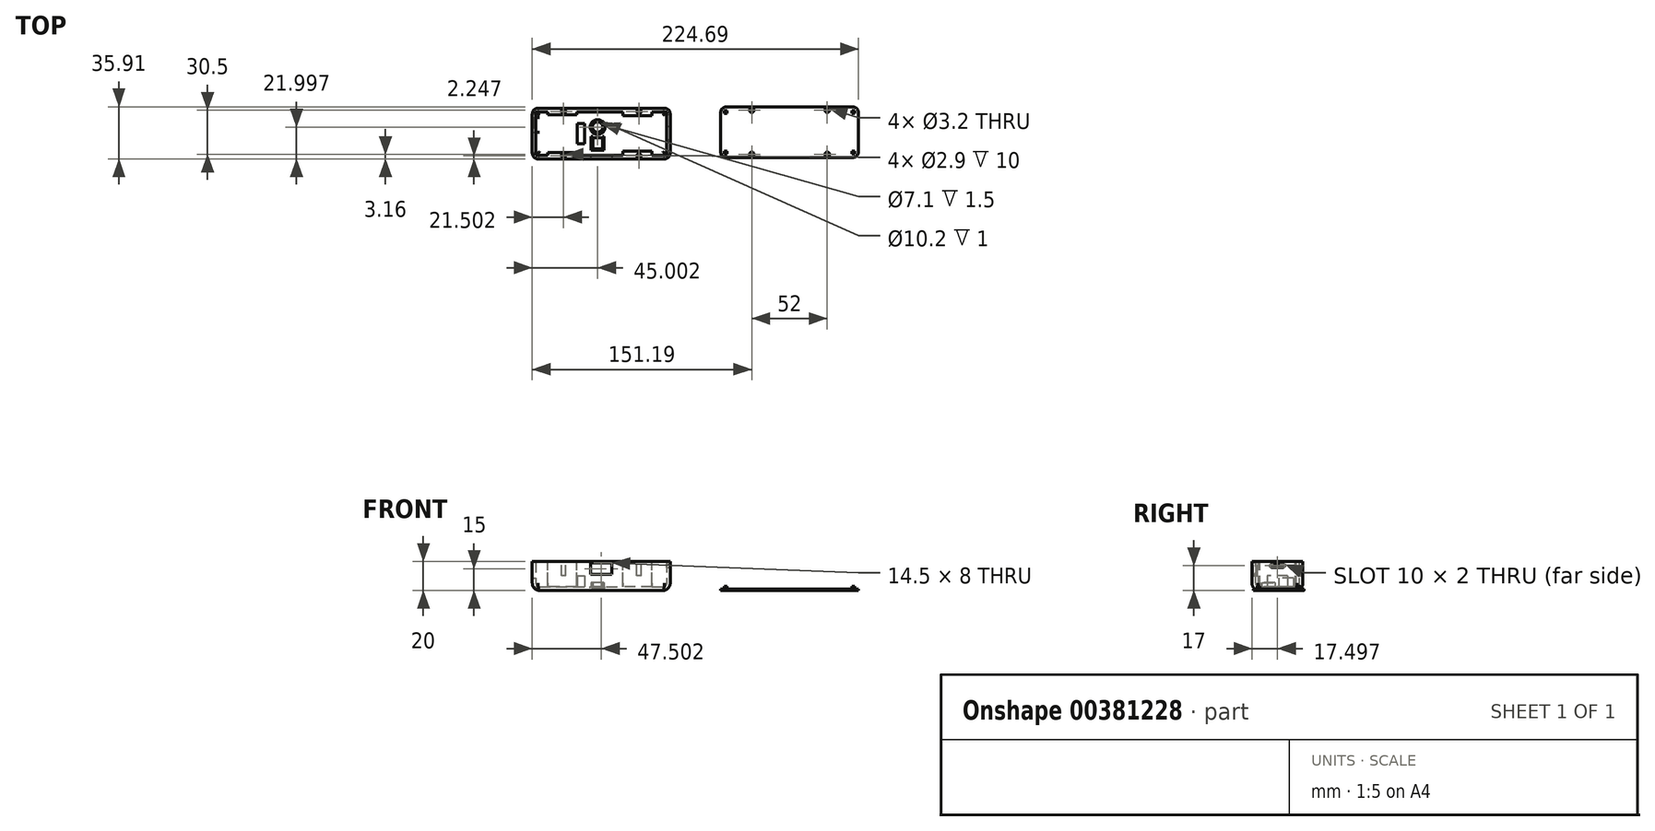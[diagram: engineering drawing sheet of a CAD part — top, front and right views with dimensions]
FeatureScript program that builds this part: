
annotation { "Feature Type Name" : "Feature", "Feature Type Description" : "" }
export const myFeature = defineFeature(function(context is Context, id is Id, definition is map)
    precondition{}
    {
        {
            var Q0;
            Q0=qCreatedBy(makeId("Top.planeOp"),FACE);
            var sketch = newSketch(context, id + "F0", { "sketchPlane" : qUnion([Q0])});
            skLineSegment(sketch, "E0.bottom", {"start": v(-57.56, 16.59) * mm, "end": v(37.44, 16.59) * mm});
            skLineSegment(sketch, "E0.top", {"start": v(-57.56, -18.41) * mm, "end": v(37.44, -18.41) * mm});
            skLineSegment(sketch, "E0.left", {"start": v(-57.56, 16.59) * mm, "end": v(-57.56, -18.41) * mm});
            skLineSegment(sketch, "E0.right", {"start": v(37.44, 16.59) * mm, "end": v(37.44, -18.41) * mm});
            skSolve(sketch);
        }
        {
            var Q0;
            Q0=makeQuery(id+"F0.imprint","IMPRINT",FACE,{"disambiguationData":[TD([[makeQuery(id+"F0.imprint","IMPRINT",EDGE,{"derivedFrom":sQuery(id+"F0.wireOp",EDGE,"E0.bottom")}),-1.0]])]});
            extrude(context, id + "F1", {"entities" : qUnion([Q0]), "depth" : 20 * mm});
        }
        {
            var Q0;
            Q0=makeQuery(id+"F1.opExtrude","CAP_FACE",FACE,{"disambiguationData":[OSD([sQuery(id+"F0.wireOp",EDGE,"E0.bottom"),sQuery(id+"F0.wireOp",EDGE,"E0.top"),sQuery(id+"F0.wireOp",EDGE,"E0.left"),sQuery(id+"F0.wireOp",EDGE,"E0.right")])],"isStart":true});
            fillet(context, id + "F2", {"entities" : qUnion([Q0]), "radius" : 5 * mm, "tangentPropagation" : true, "allowEdgeOverflow" : false});
        }
        {
            var Q0;
            Q0=makeQuery(id+"F1.opExtrude","CAP_FACE",FACE,{"disambiguationData":[OSD([sQuery(id+"F0.wireOp",EDGE,"E0.bottom"),sQuery(id+"F0.wireOp",EDGE,"E0.top"),sQuery(id+"F0.wireOp",EDGE,"E0.left"),sQuery(id+"F0.wireOp",EDGE,"E0.right")])],"isStart":false});
            shell(context, id + "F3", {"entities" : qUnion([Q0]), "thickness" : 2.5 * mm});
        }
        {
            var Q0;
            Q0=makeQuery(id+"F1.opExtrude","SWEPT_EDGE",EDGE,{"disambiguationData":[OSD([sQuery(id+"F0.wireOp",EDGE,"E0.bottom"),sQuery(id+"F0.wireOp",EDGE,"E0.left")])]});
            var Q1;
            Q1=makeQuery(id+"F1.opExtrude","SWEPT_EDGE",EDGE,{"disambiguationData":[OSD([sQuery(id+"F0.wireOp",EDGE,"E0.top"),sQuery(id+"F0.wireOp",EDGE,"E0.left")])]});
            var Q2;
            Q2=makeQuery(id+"F1.opExtrude","SWEPT_EDGE",EDGE,{"disambiguationData":[OSD([sQuery(id+"F0.wireOp",EDGE,"E0.top"),sQuery(id+"F0.wireOp",EDGE,"E0.right")])]});
            var Q3;
            Q3=makeQuery(id+"F1.opExtrude","SWEPT_EDGE",EDGE,{"disambiguationData":[OSD([sQuery(id+"F0.wireOp",EDGE,"E0.bottom"),sQuery(id+"F0.wireOp",EDGE,"E0.right")])]});
            fillet(context, id + "F4", {"entities" : qUnion([Q0, Q1, Q2, Q3]), "radius" : 4 * mm, "tangentPropagation" : true, "allowEdgeOverflow" : false});
        }
        {
            var Q0;
            Q0=makeQuery(id+"F1.opExtrude","CAP_FACE",FACE,{"disambiguationData":[OSD([sQuery(id+"F0.wireOp",EDGE,"E0.bottom"),sQuery(id+"F0.wireOp",EDGE,"E0.top"),sQuery(id+"F0.wireOp",EDGE,"E0.left"),sQuery(id+"F0.wireOp",EDGE,"E0.right")])],"isStart":false});
            var sketch = newSketch(context, id + "F5", { "sketchPlane" : qUnion([Q0])});
            skLineSegment(sketch, "E1.bottom", {"start": v(-47.06, 14.09) * mm, "end": v(-27.06, 14.09) * mm});
            skLineSegment(sketch, "E1.top", {"start": v(-47.06, 12.09) * mm, "end": v(-27.06, 12.09) * mm});
            skLineSegment(sketch, "E1.left", {"start": v(-47.06, 14.09) * mm, "end": v(-47.06, 12.09) * mm});
            skLineSegment(sketch, "E1.right", {"start": v(-27.06, 14.09) * mm, "end": v(-27.06, 12.09) * mm});
            skLineSegment(sketch, "E2.bottom", {"start": v(-47.06, -15.91) * mm, "end": v(-27.06, -15.91) * mm});
            skLineSegment(sketch, "E2.top", {"start": v(-47.06, -13.91) * mm, "end": v(-27.06, -13.91) * mm});
            skLineSegment(sketch, "E2.left", {"start": v(-47.06, -15.91) * mm, "end": v(-47.06, -13.91) * mm});
            skLineSegment(sketch, "E2.right", {"start": v(-27.06, -15.91) * mm, "end": v(-27.06, -13.91) * mm});
            skLineSegment(sketch, "E3.bottom", {"start": v(4.94, 14.09) * mm, "end": v(24.94, 14.09) * mm});
            skLineSegment(sketch, "E3.top", {"start": v(4.94, 11.34) * mm, "end": v(24.94, 11.34) * mm});
            skLineSegment(sketch, "E3.left", {"start": v(4.94, 14.09) * mm, "end": v(4.94, 11.34) * mm});
            skLineSegment(sketch, "E3.right", {"start": v(24.94, 14.09) * mm, "end": v(24.94, 11.34) * mm});
            skLineSegment(sketch, "E4.bottom", {"start": v(4.94, -15.91) * mm, "end": v(24.94, -15.91) * mm});
            skLineSegment(sketch, "E4.top", {"start": v(4.94, -13.16) * mm, "end": v(24.94, -13.16) * mm});
            skLineSegment(sketch, "E4.left", {"start": v(4.94, -15.91) * mm, "end": v(4.94, -13.16) * mm});
            skLineSegment(sketch, "E4.right", {"start": v(24.94, -15.91) * mm, "end": v(24.94, -13.16) * mm});
            skSolve(sketch);
        }
        {
            var Q0;
            Q0=makeQuery(id+"F5.imprint","IMPRINT",FACE,{"disambiguationData":[TD([[makeQuery(id+"F5.imprint","IMPRINT",EDGE,{"derivedFrom":sQuery(id+"F5.wireOp",EDGE,"E1.bottom")}),-1.0]])]});
            var Q1;
            Q1=makeQuery(id+"F5.imprint","IMPRINT",FACE,{"disambiguationData":[TD([[makeQuery(id+"F5.imprint","IMPRINT",EDGE,{"derivedFrom":sQuery(id+"F5.wireOp",EDGE,"E2.bottom")}),1.0]])]});
            var Q2;
            Q2=makeQuery(id+"F5.imprint","IMPRINT",FACE,{"disambiguationData":[TD([[makeQuery(id+"F5.imprint","IMPRINT",EDGE,{"derivedFrom":sQuery(id+"F5.wireOp",EDGE,"E4.bottom")}),1.0]])]});
            var Q3;
            Q3=makeQuery(id+"F5.imprint","IMPRINT",FACE,{"disambiguationData":[TD([[makeQuery(id+"F5.imprint","IMPRINT",EDGE,{"derivedFrom":sQuery(id+"F5.wireOp",EDGE,"E3.bottom")}),-1.0]])]});
            extrude(context, id + "F6", {"entities" : qUnion([Q0, Q1, Q2, Q3]), "operationType" : NewBodyOperationType.ADD, "endBound" : BoundingType.UP_TO_NEXT, "oppositeDirection" : true, "depth" : 25 * mm});
        }
        {
            var Q0;
            Q0=makeQuery(id+"F3.opShell","OFFSET_FACE",FACE,{"disambiguationData":[OSD([sQuery(id+"F0.wireOp",EDGE,"E0.bottom"),sQuery(id+"F0.wireOp",EDGE,"E0.top"),sQuery(id+"F0.wireOp",EDGE,"E0.left"),sQuery(id+"F0.wireOp",EDGE,"E0.right")])]});
            var sketch = newSketch(context, id + "F7", { "sketchPlane" : qUnion([Q0])});
            skLineSegment(sketch, "E5", {"start": v(-12.56, 11.59) * mm, "end": v(-12.56, -13.41) * mm, "construction": true});
            skCircle(sketch, "E6", {"center": v(-12.56, 3.59) * mm, "radius": 3.55 * mm});
            skLineSegment(sketch, "E7.bottom", {"start": v(-9.16, -11.41) * mm, "end": v(-15.96, -11.41) * mm});
            skLineSegment(sketch, "E7.top", {"start": v(-9.16, -3.71) * mm, "end": v(-15.96, -3.71) * mm});
            skLineSegment(sketch, "E7.left", {"start": v(-9.16, -11.41) * mm, "end": v(-9.16, -3.71) * mm});
            skLineSegment(sketch, "E7.right", {"start": v(-15.96, -11.41) * mm, "end": v(-15.96, -3.71) * mm});
            skPoint(sketch, "E7.middle", {"position": v(-12.56, -7.56) * mm});
            skLineSegment(sketch, "E8.bottom", {"start": v(-8.16, -2.71) * mm, "end": v(-9.16, -2.71) * mm});
            skLineSegment(sketch, "E8.top", {"start": v(-8.16, -12.41) * mm, "end": v(-16.96, -12.41) * mm});
            skLineSegment(sketch, "E8.left", {"start": v(-8.16, -2.71) * mm, "end": v(-8.16, -12.41) * mm});
            skLineSegment(sketch, "E8.right", {"start": v(-16.96, -2.71) * mm, "end": v(-16.96, -12.41) * mm});
            skLineSegment(sketch, "E9", {"start": v(-15.96, -3.71) * mm, "end": v(-15.96, -2.71) * mm});
            skLineSegment(sketch, "E10", {"start": v(-9.16, -3.71) * mm, "end": v(-9.16, -2.71) * mm});
            skLineSegment(sketch, "E11.trimOffspring", {"start": v(-15.96, -2.71) * mm, "end": v(-16.96, -2.71) * mm});
            skCircle(sketch, "E12", {"center": v(-12.56, 3.59) * mm, "radius": 5.1 * mm});
            skLineSegment(sketch, "E13.bottom", {"start": v(-26.56, 6.09) * mm, "end": v(-21.56, 6.09) * mm});
            skLineSegment(sketch, "E13.top", {"start": v(-26.56, -7.91) * mm, "end": v(-21.56, -7.91) * mm});
            skLineSegment(sketch, "E13.left", {"start": v(-26.56, 6.09) * mm, "end": v(-26.56, -7.91) * mm});
            skLineSegment(sketch, "E13.right", {"start": v(-21.56, 6.09) * mm, "end": v(-21.56, -7.91) * mm});
            skPoint(sketch, "E14", {"position": v(-26.56, -0.91) * mm});
            skPoint(sketch, "E15", {"position": v(-21.56, -0.91) * mm});
            skLineSegment(sketch, "E16", {"start": v(-52.56, -0.91) * mm, "end": v(-26.56, -0.91) * mm, "construction": true});
            skSolve(sketch);
        }
        {
            var Q0;
            Q0=makeQuery(id+"F7.imprint","IMPRINT",FACE,{"disambiguationData":[TD([[makeQuery(id+"F7.imprint","IMPRINT",EDGE,{"derivedFrom":sQuery(id+"F7.wireOp",EDGE,"E6")}),1.0]])]});
            var Q1;
            Q1=makeQuery(id+"F7.imprint","IMPRINT",FACE,{"disambiguationData":[TD([[makeQuery(id+"F7.imprint","IMPRINT",EDGE,{"derivedFrom":sQuery(id+"F7.wireOp",EDGE,"E7.bottom")}),-1.0]])]});
            extrude(context, id + "F8", {"entities" : qUnion([Q0, Q1]), "operationType" : NewBodyOperationType.REMOVE, "endBound" : BoundingType.UP_TO_NEXT, "oppositeDirection" : true, "depth" : 25 * mm});
        }
        {
            var Q0;
            Q0=makeQuery(id+"F7.imprint","IMPRINT",FACE,{"disambiguationData":[TD([[makeQuery(id+"F7.imprint","IMPRINT",EDGE,{"derivedFrom":sQuery(id+"F7.wireOp",EDGE,"E6")}),-1.0]])]});
            extrude(context, id + "F9", {"entities" : qUnion([Q0]), "operationType" : NewBodyOperationType.REMOVE, "oppositeDirection" : true, "depth" : 1 * mm});
        }
        {
            var Q0;
            Q0=makeQuery(id+"F7.imprint","IMPRINT",FACE,{"disambiguationData":[TD([[makeQuery(id+"F7.imprint","IMPRINT",EDGE,{"derivedFrom":sQuery(id+"F7.wireOp",EDGE,"E7.bottom")}),1.0]])]});
            extrude(context, id + "F10", {"entities" : qUnion([Q0]), "operationType" : NewBodyOperationType.ADD, "depth" : 3 * mm});
        }
        {
            var Q0;
            Q0=makeQuery(id+"F7.imprint","IMPRINT",FACE,{"disambiguationData":[TD([[makeQuery(id+"F7.imprint","IMPRINT",EDGE,{"derivedFrom":sQuery(id+"F7.wireOp",EDGE,"E13.bottom")}),-1.0]])]});
            extrude(context, id + "F11", {"entities" : qUnion([Q0]), "operationType" : NewBodyOperationType.ADD, "depth" : 7.6 * mm});
        }
        {
            var Q0;
            Q0=makeQuery(id+"F6.opExtrude","SWEPT_FACE",FACE,{"disambiguationData":[OSD([sQuery(id+"F5.wireOp",EDGE,"E1.left")])]});
            var sketch = newSketch(context, id + "F12", { "sketchPlane" : qUnion([Q0])});
            skLineSegment(sketch, "E17.bottom", {"start": v(-10.09, 8.5) * mm, "end": v(-0.09, 8.5) * mm});
            skLineSegment(sketch, "E17.top", {"start": v(-10.09, 2.5) * mm, "end": v(-0.09, 2.5) * mm});
            skLineSegment(sketch, "E17.left", {"start": v(-10.09, 8.5) * mm, "end": v(-10.09, 2.5) * mm});
            skLineSegment(sketch, "E17.right", {"start": v(-0.09, 8.5) * mm, "end": v(-0.09, 2.5) * mm});
            skSolve(sketch);
        }
        {
            var Q0;
            Q0=makeQuery(id+"F12.imprint","IMPRINT",FACE,{"disambiguationData":[TD([[makeQuery(id+"F12.imprint","IMPRINT",EDGE,{"derivedFrom":sQuery(id+"F12.wireOp",EDGE,"E17.bottom")}),-1.0]])]});
            extrude(context, id + "F13", {"entities" : qUnion([Q0]), "operationType" : NewBodyOperationType.REMOVE, "depth" : 13.3 * mm});
        }
        {
            var Q0;
            Q0=makeQuery(id+"F1.opExtrude","SWEPT_FACE",FACE,{"disambiguationData":[OSD([sQuery(id+"F0.wireOp",EDGE,"E0.right")])]});
            var sketch = newSketch(context, id + "F14", { "sketchPlane" : qUnion([Q0])});
            skLineSegment(sketch, "E18", {"start": v(12.59, 17) * mm, "end": v(-14.41, 17) * mm, "construction": true});
            skArc(sketch, "E19", {"start": v(3.09, 16) * mm, "mid": v(4.09, 17) * mm, "end": v(3.09, 18) * mm});
            skArc(sketch, "E20", {"start": v(-4.91, 18) * mm, "mid": v(-5.91, 16.97) * mm, "end": v(-4.86, 16) * mm});
            skLineSegment(sketch, "E21", {"start": v(3.09, 18) * mm, "end": v(-4.91, 18) * mm});
            skLineSegment(sketch, "E22", {"start": v(-4.97, 16) * mm, "end": v(3.09, 16) * mm});
            skLineSegment(sketch, "E23", {"start": v(-0.91, 18) * mm, "end": v(-0.91, 20) * mm, "construction": true});
            skSolve(sketch);
        }
        {
            var Q0;
            {var subQ5=sQuery(id+"F14.wireOp",EDGE,"E19");Q0=makeQuery(id+"F14.imprint","IMPRINT",FACE,{"disambiguationData":[TD([[makeQuery(id+"F14.imprint","IMPRINT",EDGE,{"derivedFrom":subQ5}),1.0]])]});}
            extrude(context, id + "F15", {"entities" : qUnion([Q0]), "operationType" : NewBodyOperationType.REMOVE, "endBound" : BoundingType.UP_TO_NEXT, "oppositeDirection" : true, "depth" : 25 * mm});
        }
        {
            var Q0;
            Q0=makeQuery(id+"F6.boolean.opBoolean","MERGE",FACE,{"derivedFrom":[makeQuery(id+"F1.opExtrude","CAP_FACE",FACE,{"disambiguationData":[OSD([sQuery(id+"F0.wireOp",EDGE,"E0.bottom"),sQuery(id+"F0.wireOp",EDGE,"E0.top"),sQuery(id+"F0.wireOp",EDGE,"E0.left"),sQuery(id+"F0.wireOp",EDGE,"E0.right")])],"isStart":false}),makeQuery(id+"F6.opExtrude","CAP_FACE",FACE,{"disambiguationData":[OSD([sQuery(id+"F5.wireOp",EDGE,"E1.bottom"),sQuery(id+"F5.wireOp",EDGE,"E1.top"),sQuery(id+"F5.wireOp",EDGE,"E1.left"),sQuery(id+"F5.wireOp",EDGE,"E1.right")])],"isStart":true}),makeQuery(id+"F6.opExtrude","CAP_FACE",FACE,{"disambiguationData":[OSD([sQuery(id+"F5.wireOp",EDGE,"E2.bottom"),sQuery(id+"F5.wireOp",EDGE,"E2.top"),sQuery(id+"F5.wireOp",EDGE,"E2.left"),sQuery(id+"F5.wireOp",EDGE,"E2.right")])],"isStart":true}),makeQuery(id+"F6.opExtrude","CAP_FACE",FACE,{"disambiguationData":[OSD([sQuery(id+"F5.wireOp",EDGE,"E3.bottom"),sQuery(id+"F5.wireOp",EDGE,"E3.top"),sQuery(id+"F5.wireOp",EDGE,"E3.left"),sQuery(id+"F5.wireOp",EDGE,"E3.right")])],"isStart":true}),makeQuery(id+"F6.opExtrude","CAP_FACE",FACE,{"disambiguationData":[OSD([sQuery(id+"F5.wireOp",EDGE,"E4.bottom"),sQuery(id+"F5.wireOp",EDGE,"E4.top"),sQuery(id+"F5.wireOp",EDGE,"E4.left"),sQuery(id+"F5.wireOp",EDGE,"E4.right")])],"isStart":true})]});
            var sketch = newSketch(context, id + "F16", { "sketchPlane" : qUnion([Q0])});
            skCircle(sketch, "E24", {"center": v(-36.06, 14.34) * mm, "radius": 1.45 * mm});
            skCircle(sketch, "E25", {"center": v(-36.06, -16.16) * mm, "radius": 1.45 * mm});
            skCircle(sketch, "E26", {"center": v(15.94, -16.16) * mm, "radius": 1.45 * mm});
            skCircle(sketch, "E27", {"center": v(15.94, 14.34) * mm, "radius": 1.45 * mm});
            skLineSegment(sketch, "E28", {"start": v(-36.06, 14.34) * mm, "end": v(-36.06, -16.16) * mm, "construction": true});
            skLineSegment(sketch, "E29", {"start": v(15.94, 14.34) * mm, "end": v(15.94, -16.16) * mm, "construction": true});
            skLineSegment(sketch, "E30", {"start": v(-10.06, 16.59) * mm, "end": v(-10.06, -18.41) * mm, "construction": true});
            skLineSegment(sketch, "E31", {"start": v(-36.06, 14.34) * mm, "end": v(15.94, 14.34) * mm, "construction": true});
            skLineSegment(sketch, "E32", {"start": v(-36.06, -16.16) * mm, "end": v(15.94, -16.16) * mm, "construction": true});
            skLineSegment(sketch, "E33", {"start": v(-36.06, 14.34) * mm, "end": v(-36.06, 16.59) * mm, "construction": true});
            skLineSegment(sketch, "E34", {"start": v(-36.06, -16.16) * mm, "end": v(-36.06, -18.41) * mm, "construction": true});
            skSolve(sketch);
        }
        {
            var Q0;
            Q0=makeQuery(id+"F16.imprint","IMPRINT",FACE,{"disambiguationData":[TD([[makeQuery(id+"F16.imprint","IMPRINT",EDGE,{"derivedFrom":sQuery(id+"F16.wireOp",EDGE,"E24")}),1.0]])]});
            var Q1;
            Q1=makeQuery(id+"F16.imprint","IMPRINT",FACE,{"disambiguationData":[TD([[makeQuery(id+"F16.imprint","IMPRINT",EDGE,{"derivedFrom":sQuery(id+"F16.wireOp",EDGE,"E25")}),1.0]])]});
            var Q2;
            Q2=makeQuery(id+"F16.imprint","IMPRINT",FACE,{"disambiguationData":[TD([[makeQuery(id+"F16.imprint","IMPRINT",EDGE,{"derivedFrom":sQuery(id+"F16.wireOp",EDGE,"E26")}),1.0]])]});
            var Q3;
            Q3=makeQuery(id+"F16.imprint","IMPRINT",FACE,{"disambiguationData":[TD([[makeQuery(id+"F16.imprint","IMPRINT",EDGE,{"derivedFrom":sQuery(id+"F16.wireOp",EDGE,"E27")}),1.0]])]});
            extrude(context, id + "F17", {"entities" : qUnion([Q0, Q1, Q2, Q3]), "operationType" : NewBodyOperationType.REMOVE, "oppositeDirection" : true, "depth" : 10 * mm});
        }
        {
            var Q0;
            Q0=makeQuery(id+"F1.opExtrude","SWEPT_FACE",FACE,{"disambiguationData":[OSD([sQuery(id+"F0.wireOp",EDGE,"E0.top")])]});
            var sketch = newSketch(context, id + "F18", { "sketchPlane" : qUnion([Q0])});
            skLineSegment(sketch, "E35", {"start": v(-10.06, 20) * mm, "end": v(-10.06, 5) * mm, "construction": true});
            skLineSegment(sketch, "E36.bottom", {"start": v(-2.8, 19) * mm, "end": v(-17.3, 19) * mm});
            skLineSegment(sketch, "E36.top", {"start": v(-2.8, 11) * mm, "end": v(-17.3, 11) * mm});
            skLineSegment(sketch, "E36.left", {"start": v(-2.8, 19) * mm, "end": v(-2.8, 11) * mm});
            skLineSegment(sketch, "E36.right", {"start": v(-17.3, 19) * mm, "end": v(-17.3, 11) * mm});
            skPoint(sketch, "E36.middle", {"position": v(-10.06, 15) * mm});
            skSolve(sketch);
        }
        {
            var Q0;
            Q0 = qSketchRegion(id + "F18", true);
            extrude(context, id + "F19", {"entities" : qUnion([Q0]), "operationType" : NewBodyOperationType.REMOVE, "endBound" : BoundingType.UP_TO_NEXT, "oppositeDirection" : true, "depth" : 25 * mm});
        }
        {
            var Q0;
            Q0=qCreatedBy(makeId("Top.planeOp"),FACE);
            var sketch = newSketch(context, id + "F20", { "sketchPlane" : qUnion([Q0])});
            skLineSegment(sketch, "E37.bottom", {"start": v(76.13, 17.5) * mm, "end": v(163.13, 17.5) * mm});
            skLineSegment(sketch, "E37.top", {"start": v(76.13, -17.5) * mm, "end": v(163.13, -17.5) * mm});
            skLineSegment(sketch, "E37.left", {"start": v(72.13, 13.5) * mm, "end": v(72.13, -13.5) * mm});
            skLineSegment(sketch, "E37.right", {"start": v(167.13, 13.5) * mm, "end": v(167.13, -13.5) * mm});
            skPoint(sketch, "E37.middle", {"position": v(119.63, 0) * mm});
            skPoint(sketch, "E38.visualSharp", {"position": v(72.13, 17.5) * mm});
            skArc(sketch, "E38.filletArc", {"start": v(76.13, 17.5) * mm, "mid": v(73.3, 16.33) * mm, "end": v(72.13, 13.5) * mm});
            skPoint(sketch, "E39.visualSharp", {"position": v(72.13, -17.5) * mm});
            skArc(sketch, "E39.filletArc", {"start": v(72.13, -13.5) * mm, "mid": v(73.3, -16.33) * mm, "end": v(76.13, -17.5) * mm});
            skPoint(sketch, "E40.visualSharp", {"position": v(167.13, -17.5) * mm});
            skArc(sketch, "E40.filletArc", {"start": v(163.13, -17.5) * mm, "mid": v(165.96, -16.33) * mm, "end": v(167.13, -13.5) * mm});
            skPoint(sketch, "E41.visualSharp", {"position": v(167.13, 17.5) * mm});
            skArc(sketch, "E41.filletArc", {"start": v(167.13, 13.5) * mm, "mid": v(165.96, 16.33) * mm, "end": v(163.13, 17.5) * mm});
            skSolve(sketch);
        }
        {
            var Q0;
            Q0=makeQuery(id+"F20.imprint","IMPRINT",FACE,{"disambiguationData":[TD([[makeQuery(id+"F20.imprint","IMPRINT",EDGE,{"derivedFrom":sQuery(id+"F20.wireOp",EDGE,"E37.bottom")}),-1.0]])]});
            extrude(context, id + "F21", {"entities" : qUnion([Q0]), "depth" : 1 * mm});
        }
        {
            var Q0;
            Q0=makeQuery(id+"F21.opExtrude","CAP_FACE",FACE,{"disambiguationData":[OSD([sQuery(id+"F20.wireOp",EDGE,"E37.bottom"),sQuery(id+"F20.wireOp",EDGE,"E37.top"),sQuery(id+"F20.wireOp",EDGE,"E37.left"),sQuery(id+"F20.wireOp",EDGE,"E37.right"),sQuery(id+"F20.wireOp",EDGE,"E38.filletArc"),sQuery(id+"F20.wireOp",EDGE,"E39.filletArc"),sQuery(id+"F20.wireOp",EDGE,"E40.filletArc"),sQuery(id+"F20.wireOp",EDGE,"E41.filletArc")])],"isStart":false});
            var sketch = newSketch(context, id + "F22", { "sketchPlane" : qUnion([Q0])});
            skLineSegment(sketch, "E42.bottom", {"start": v(74.73, 14.9) * mm, "end": v(76.73, 14.9) * mm});
            skLineSegment(sketch, "E42.top", {"start": v(74.73, 12.9) * mm, "end": v(76.73, 12.9) * mm});
            skLineSegment(sketch, "E42.left", {"start": v(74.73, 14.9) * mm, "end": v(74.73, 12.9) * mm});
            skLineSegment(sketch, "E42.right", {"start": v(76.73, 14.9) * mm, "end": v(76.73, 12.9) * mm});
            skLineSegment(sketch, "E43.bottom", {"start": v(74.73, -14.9) * mm, "end": v(76.73, -14.9) * mm});
            skLineSegment(sketch, "E43.top", {"start": v(74.73, -12.9) * mm, "end": v(76.73, -12.9) * mm});
            skLineSegment(sketch, "E43.left", {"start": v(74.73, -14.9) * mm, "end": v(74.73, -12.9) * mm});
            skLineSegment(sketch, "E43.right", {"start": v(76.73, -14.9) * mm, "end": v(76.73, -12.9) * mm});
            skLineSegment(sketch, "E44.bottom", {"start": v(164.53, -14.9) * mm, "end": v(162.53, -14.9) * mm});
            skLineSegment(sketch, "E44.top", {"start": v(164.53, -12.9) * mm, "end": v(162.53, -12.9) * mm});
            skLineSegment(sketch, "E44.left", {"start": v(164.53, -14.9) * mm, "end": v(164.53, -12.9) * mm});
            skLineSegment(sketch, "E44.right", {"start": v(162.53, -14.9) * mm, "end": v(162.53, -12.9) * mm});
            skLineSegment(sketch, "E45.bottom", {"start": v(164.53, 14.9) * mm, "end": v(162.53, 14.9) * mm});
            skLineSegment(sketch, "E45.top", {"start": v(164.53, 12.9) * mm, "end": v(162.53, 12.9) * mm});
            skLineSegment(sketch, "E45.left", {"start": v(164.53, 14.9) * mm, "end": v(164.53, 12.9) * mm});
            skLineSegment(sketch, "E45.right", {"start": v(162.53, 14.9) * mm, "end": v(162.53, 12.9) * mm});
            skLineSegment(sketch, "E46", {"start": v(76.73, 14.9) * mm, "end": v(162.53, 14.9) * mm, "construction": true});
            skLineSegment(sketch, "E47", {"start": v(76.73, -14.9) * mm, "end": v(162.53, -14.9) * mm, "construction": true});
            skLineSegment(sketch, "E48", {"start": v(74.73, 12.9) * mm, "end": v(74.73, -12.9) * mm, "construction": true});
            skLineSegment(sketch, "E49", {"start": v(164.53, 12.9) * mm, "end": v(164.53, -12.9) * mm, "construction": true});
            skSolve(sketch);
        }
        {
            var Q0;
            Q0=makeQuery(id+"F22.imprint","IMPRINT",FACE,{"disambiguationData":[TD([[makeQuery(id+"F22.imprint","IMPRINT",EDGE,{"derivedFrom":sQuery(id+"F22.wireOp",EDGE,"E42.bottom")}),-1.0]])]});
            var Q1;
            Q1=makeQuery(id+"F22.imprint","IMPRINT",FACE,{"disambiguationData":[TD([[makeQuery(id+"F22.imprint","IMPRINT",EDGE,{"derivedFrom":sQuery(id+"F22.wireOp",EDGE,"E43.bottom")}),1.0]])]});
            var Q2;
            Q2=makeQuery(id+"F22.imprint","IMPRINT",FACE,{"disambiguationData":[TD([[makeQuery(id+"F22.imprint","IMPRINT",EDGE,{"derivedFrom":sQuery(id+"F22.wireOp",EDGE,"E44.bottom")}),-1.0]])]});
            var Q3;
            Q3=makeQuery(id+"F22.imprint","IMPRINT",FACE,{"disambiguationData":[TD([[makeQuery(id+"F22.imprint","IMPRINT",EDGE,{"derivedFrom":sQuery(id+"F22.wireOp",EDGE,"E45.bottom")}),1.0]])]});
            extrude(context, id + "F23", {"entities" : qUnion([Q0, Q1, Q2, Q3]), "operationType" : NewBodyOperationType.ADD, "depth" : 2 * mm});
        }
        {
            var Q0;
            Q0=makeQuery(id+"F21.opExtrude","CAP_FACE",FACE,{"disambiguationData":[OSD([sQuery(id+"F20.wireOp",EDGE,"E37.bottom"),sQuery(id+"F20.wireOp",EDGE,"E37.top"),sQuery(id+"F20.wireOp",EDGE,"E37.left"),sQuery(id+"F20.wireOp",EDGE,"E37.right"),sQuery(id+"F20.wireOp",EDGE,"E38.filletArc"),sQuery(id+"F20.wireOp",EDGE,"E39.filletArc"),sQuery(id+"F20.wireOp",EDGE,"E40.filletArc"),sQuery(id+"F20.wireOp",EDGE,"E41.filletArc")])],"isStart":false});
            var sketch = newSketch(context, id + "F24", { "sketchPlane" : qUnion([Q0])});
            skLineSegment(sketch, "E50", {"start": v(119.63, 17.5) * mm, "end": v(119.63, -17.5) * mm, "construction": true});
            skLineSegment(sketch, "E51", {"start": v(93.63, 15.25) * mm, "end": v(145.63, 15.25) * mm, "construction": true});
            skLineSegment(sketch, "E52", {"start": v(145.63, 15.25) * mm, "end": v(145.63, -15.25) * mm, "construction": true});
            skLineSegment(sketch, "E53", {"start": v(145.63, -15.25) * mm, "end": v(93.63, -15.25) * mm, "construction": true});
            skLineSegment(sketch, "E54", {"start": v(93.63, -15.25) * mm, "end": v(93.63, 15.25) * mm, "construction": true});
            skCircle(sketch, "E55", {"center": v(93.63, 15.25) * mm, "radius": 1.6 * mm});
            skCircle(sketch, "E56", {"center": v(93.63, -15.25) * mm, "radius": 1.6 * mm});
            skCircle(sketch, "E57", {"center": v(145.63, -15.25) * mm, "radius": 1.6 * mm});
            skCircle(sketch, "E58", {"center": v(145.63, 15.25) * mm, "radius": 1.6 * mm});
            skLineSegment(sketch, "E59", {"start": v(93.63, 15.25) * mm, "end": v(93.63, 17.5) * mm, "construction": true});
            skLineSegment(sketch, "E60", {"start": v(93.63, -15.25) * mm, "end": v(93.63, -17.5) * mm, "construction": true});
            skSolve(sketch);
        }
        {
            var Q0;
            Q0=makeQuery(id+"F24.imprint","IMPRINT",FACE,{"disambiguationData":[TD([[makeQuery(id+"F24.imprint","IMPRINT",EDGE,{"derivedFrom":sQuery(id+"F24.wireOp",EDGE,"E55")}),1.0]])]});
            var Q1;
            Q1=makeQuery(id+"F24.imprint","IMPRINT",FACE,{"disambiguationData":[TD([[makeQuery(id+"F24.imprint","IMPRINT",EDGE,{"derivedFrom":sQuery(id+"F24.wireOp",EDGE,"E56")}),1.0]])]});
            var Q2;
            Q2=makeQuery(id+"F24.imprint","IMPRINT",FACE,{"disambiguationData":[TD([[makeQuery(id+"F24.imprint","IMPRINT",EDGE,{"derivedFrom":sQuery(id+"F24.wireOp",EDGE,"E57")}),1.0]])]});
            var Q3;
            Q3=makeQuery(id+"F24.imprint","IMPRINT",FACE,{"disambiguationData":[TD([[makeQuery(id+"F24.imprint","IMPRINT",EDGE,{"derivedFrom":sQuery(id+"F24.wireOp",EDGE,"E58")}),1.0]])]});
            extrude(context, id + "F25", {"entities" : qUnion([Q0, Q1, Q2, Q3]), "operationType" : NewBodyOperationType.REMOVE, "endBound" : BoundingType.UP_TO_NEXT, "oppositeDirection" : true, "depth" : 25 * mm});
        }
    });
